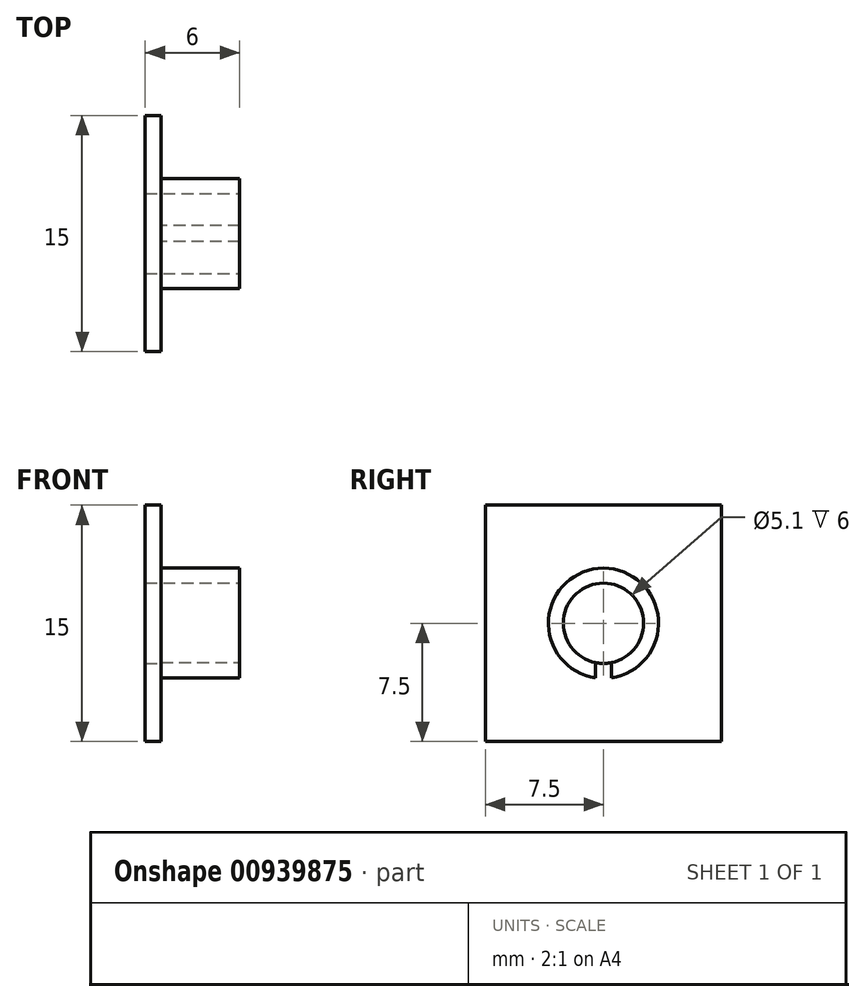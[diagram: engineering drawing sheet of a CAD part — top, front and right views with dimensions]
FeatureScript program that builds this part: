
annotation { "Feature Type Name" : "Feature", "Feature Type Description" : "" }
export const myFeature = defineFeature(function(context is Context, id is Id, definition is map)
    precondition{}
    {
        {
            var Q0;
            Q0=qCreatedBy(makeId("Right.planeOp"),FACE);
            var sketch = newSketch(context, id + "F0", { "sketchPlane" : qUnion([Q0])});
            skLineSegment(sketch, "E0.bottom", {"start": v(-7.5, 7.5) * mm, "end": v(7.5, 7.5) * mm});
            skLineSegment(sketch, "E0.top", {"start": v(-7.5, -7.5) * mm, "end": v(7.5, -7.5) * mm});
            skLineSegment(sketch, "E0.left", {"start": v(-7.5, 7.5) * mm, "end": v(-7.5, -7.5) * mm});
            skLineSegment(sketch, "E0.right", {"start": v(7.5, 7.5) * mm, "end": v(7.5, -7.5) * mm});
            skPoint(sketch, "E0.middle", {"position": v(0, 0) * mm});
            skSolve(sketch);
        }
        {
            var Q0;
            Q0 = qSketchRegion(id + "F0", true);
            extrude(context, id + "F1", {"entities" : qUnion([Q0]), "depth" : 1 * mm, "offsetDistance" : 25 * mm});
        }
        {
            var Q0;
            Q0=makeQuery(id+"F1.opExtrude","CAP_FACE",FACE,{"disambiguationData":[OSD([sQuery(id+"F0.wireOp",EDGE,"E0.bottom"),sQuery(id+"F0.wireOp",EDGE,"E0.top"),sQuery(id+"F0.wireOp",EDGE,"E0.left"),sQuery(id+"F0.wireOp",EDGE,"E0.right")])],"isStart":false});
            var sketch = newSketch(context, id + "F2", { "sketchPlane" : qUnion([Q0])});
            skCircle(sketch, "E1", {"center": v(0, 0) * mm, "radius": 3.5 * mm});
            skSolve(sketch);
        }
        {
            var Q0;
            Q0 = qSketchRegion(id + "F2", true);
            extrude(context, id + "F3", {"entities" : qUnion([Q0]), "operationType" : NewBodyOperationType.ADD, "depth" : 5 * mm, "offsetDistance" : 25 * mm});
        }
        {
            var Q0;
            Q0=makeQuery(id+"F3.opExtrude","CAP_FACE",FACE,{"disambiguationData":[OSD([sQuery(id+"F2.wireOp",EDGE,"E1")])],"isStart":false});
            var sketch = newSketch(context, id + "F4", { "sketchPlane" : qUnion([Q0])});
            skCircle(sketch, "E2", {"center": v(0, 0) * mm, "radius": 2.55 * mm});
            skSolve(sketch);
        }
        {
            var Q0;
            Q0 = qSketchRegion(id + "F4", true);
            extrude(context, id + "F5", {"entities" : qUnion([Q0]), "operationType" : NewBodyOperationType.REMOVE, "oppositeDirection" : true, "depth" : 25 * mm, "offsetDistance" : 25 * mm});
        }
        {
            var Q0;
            Q0=makeQuery(id+"F1.opExtrude","SWEPT_FACE",FACE,{"disambiguationData":[OSD([sQuery(id+"F0.wireOp",EDGE,"E0.top")])]});
            var sketch = newSketch(context, id + "F6", { "sketchPlane" : qUnion([Q0])});
            skLineSegment(sketch, "E3.bottom", {"start": v(1, 0.5) * mm, "end": v(6.5, 0.5) * mm});
            skLineSegment(sketch, "E3.top", {"start": v(1, -0.5) * mm, "end": v(6.5, -0.5) * mm});
            skLineSegment(sketch, "E3.left", {"start": v(1, 0.5) * mm, "end": v(1, -0.5) * mm});
            skLineSegment(sketch, "E3.right", {"start": v(6.5, 0.5) * mm, "end": v(6.5, -0.5) * mm});
            skSolve(sketch);
        }
        {
            var Q0;
            Q0 = qSketchRegion(id + "F6", true);
            extrude(context, id + "F7", {"entities" : qUnion([Q0]), "operationType" : NewBodyOperationType.REMOVE, "oppositeDirection" : true, "depth" : 7 * mm, "offsetDistance" : 25 * mm});
        }
    });
